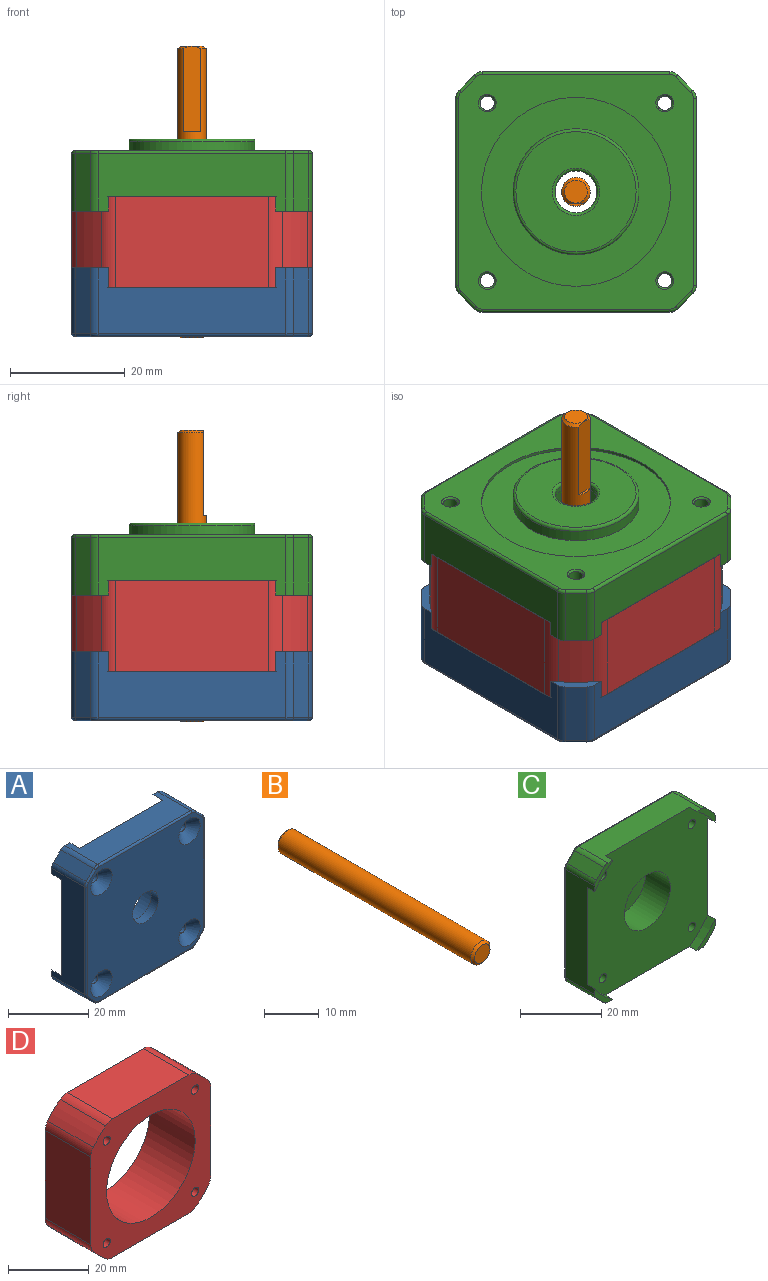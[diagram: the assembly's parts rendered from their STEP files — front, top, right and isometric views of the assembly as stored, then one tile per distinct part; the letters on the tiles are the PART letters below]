
ASSEMBLY  parts=4 mates=2
PART A: 53 faces, bbox 42.3x12x42.3 mm
  f0: cylinder r=4.5mm len=9mm, axis (0,-1,0), area 70.7mm2, adj f10,f28
  f1: plane 32.74x11.5mm, normal (0,0,1), area 274.1mm2, adj f9,f11,f13,f14,f16,f30,f31,f50
  f2: plane 32.74x11.5mm, normal (1,0,0), area 274.1mm2, adj f9,f11,f13,f20,f22,f29,f36,f42
  f3: plane 32.74x11.5mm, normal (0,0,-1), area 274.1mm2, adj f9,f17,f19,f20,f22,f34,f35,f39
  f4: plane 32.74x11.5mm, normal (-1,0,0), area 274.1mm2, adj f9,f14,f16,f17,f19,f32,f33,f47
  f5: cylinder r=1.25mm len=6mm, axis (0,-1,0), area 47.1mm2, adj f9,f26
  f6: cylinder r=1.25mm len=6mm, axis (0,-1,0), area 47.1mm2, adj f9,f25
  f7: cylinder r=1.25mm len=6mm, axis (0,-1,0), area 47.1mm2, adj f9,f24
  f8: cylinder r=1.25mm len=6mm, axis (0,-1,0), area 47.1mm2, adj f9,f23
  f9: plane 42x42mm, normal (0,1,0), area 1472mm2, adj f1,f2,f3,f4,f5,f6,f7,f8
  f10: plane 41x41mm, normal (0,-1,0), area 1415.7mm2, adj f0,f23,f24,f25,f26,f37,f38,f39
  f11: cylinder r=25.6mm len=6.36mm, axis (0,-1,0), area 31.6mm2, adj f1,f2,f9,f13
  f12: plane 11.5x2.63mm, normal (0.71,0,0.71), area 42.7mm2, adj f13,f29,f30,f46
  f13: plane 6.36x6.36mm, normal (0,1,0), area 10.4mm2, adj f1,f2,f11,f12,f29,f30
  f14: cylinder r=25.6mm len=6.36mm, axis (0,-1,0), area 31.6mm2, adj f1,f4,f9,f16
  f15: plane 11.5x2.63mm, normal (-0.71,0,0.71), area 42.7mm2, adj f16,f31,f32,f51
  f16: plane 6.36x6.36mm, normal (0,1,0), area 10.4mm2, adj f1,f4,f14,f15,f31,f32
  f17: cylinder r=25.6mm len=6.36mm, axis (0,-1,0), area 31.6mm2, adj f3,f4,f9,f19
  f18: plane 11.5x2.63mm, normal (-0.71,0,-0.71), area 42.7mm2, adj f19,f33,f34,f43
  f19: plane 6.36x6.36mm, normal (0,1,0), area 10.4mm2, adj f3,f4,f17,f18,f33,f34
  f20: cylinder r=25.6mm len=6.36mm, axis (0,-1,0), area 31.6mm2, adj f2,f3,f9,f22
  f21: plane 11.5x2.63mm, normal (0.71,0,-0.71), area 42.7mm2, adj f22,f35,f36,f38
  f22: plane 6.36x6.36mm, normal (0,1,0), area 10.4mm2, adj f2,f3,f20,f21,f35,f36
  f23: cone r=3.75mm half-angle=45deg, axis (0,-1,0), area 55.5mm2, adj f8,f10
  f24: cone r=3.75mm half-angle=45deg, axis (0,-1,0), area 55.5mm2, adj f7,f10
  f25: cone r=3.75mm half-angle=45deg, axis (0,-1,0), area 55.5mm2, adj f6,f10
  f26: cone r=3.75mm half-angle=45deg, axis (0,-1,0), area 55.5mm2, adj f5,f10
  f27: cylinder r=8mm len=16mm, axis (0,1,0), area 301.6mm2, adj f9,f28
  f28: plane 16x16mm, normal (0,1,0), area 137.4mm2, adj f0,f27
  f29: cylinder r=2mm len=11.5mm, axis (0,-1,0), area 18.1mm2, adj f2,f12,f13,f44
  f30: cylinder r=2mm len=11.5mm, axis (0,-1,0), area 18.1mm2, adj f1,f12,f13,f48
  f31: cylinder r=2mm len=11.5mm, axis (0,-1,0), area 18.1mm2, adj f1,f15,f16,f52
  f32: cylinder r=2mm len=11.5mm, axis (0,1,0), area 18.1mm2, adj f4,f15,f16,f49
  f33: cylinder r=2mm len=11.5mm, axis (0,-1,0), area 18.1mm2, adj f4,f18,f19,f45
  f34: cylinder r=2mm len=11.5mm, axis (0,-1,0), area 18.1mm2, adj f3,f18,f19,f41
  f35: cylinder r=2mm len=11.5mm, axis (0,-1,0), area 18.1mm2, adj f3,f21,f22,f37
  f36: cylinder r=2mm len=11.5mm, axis (0,1,0), area 18.1mm2, adj f2,f21,f22,f40
  f37: torus R=1.5mm, axis (0,1,0), area 1.1mm2, adj f10,f35,f38,f39
  f38: cylinder r=0.5mm len=2.98mm, axis (-0.71,0,-0.71), area 2.9mm2, adj f10,f21,f37,f40
  f39: cylinder r=0.5mm len=32.74mm, axis (-1,0,0), area 25.7mm2, adj f3,f10,f37,f41
  f40: torus R=1.5mm, axis (0,1,0), area 1.1mm2, adj f10,f36,f38,f42
  f41: torus R=1.5mm, axis (0,1,0), area 1.1mm2, adj f10,f34,f39,f43
  f42: cylinder r=0.5mm len=32.74mm, axis (0,0,-1), area 25.7mm2, adj f2,f10,f40,f44
  f43: cylinder r=0.5mm len=2.98mm, axis (-0.71,0,0.71), area 2.9mm2, adj f10,f18,f41,f45
  f44: torus R=1.5mm, axis (0,1,0), area 1.1mm2, adj f10,f29,f42,f46
  f45: torus R=1.5mm, axis (0,1,0), area 1.1mm2, adj f10,f33,f43,f47
  f46: cylinder r=0.5mm len=2.98mm, axis (0.71,0,-0.71), area 2.9mm2, adj f10,f12,f44,f48
  f47: cylinder r=0.5mm len=32.74mm, axis (0,0,1), area 25.7mm2, adj f4,f10,f45,f49
  f48: torus R=1.5mm, axis (0,1,0), area 1.1mm2, adj f10,f30,f46,f50
  f49: torus R=1.5mm, axis (0,1,0), area 1.1mm2, adj f10,f32,f47,f51
  f50: cylinder r=0.5mm len=32.74mm, axis (1,0,0), area 25.7mm2, adj f1,f10,f48,f52
  f51: cylinder r=0.5mm len=2.98mm, axis (0.71,0,0.71), area 2.9mm2, adj f10,f15,f49,f52
  f52: torus R=1.5mm, axis (0,1,0), area 1.1mm2, adj f10,f31,f50,f51
PART B: 7 faces, bbox 5x51x5 mm
  f0: cylinder r=2.5mm len=50mm, axis (0,-1,0), area 738.7mm2, adj f3,f4,f5,f6
  f1: plane 4x4mm, normal (0,1,0), area 12.6mm2, adj f6
  f2: plane 4x4mm, normal (0,-1,0), area 12.6mm2, adj f5
  f3: plane 15x3mm, normal (0,0,-1), area 44.5mm2, adj f0,f4,f6
  f4: plane 3x0.5mm, normal (0,1,0), area 1mm2, adj f0,f3
  f5: cone r=2.5mm half-angle=45deg, axis (0,1,0), area 10mm2, adj f0,f2
  f6: cone r=2mm half-angle=45deg, axis (0,-1,0), area 8.6mm2, adj f0,f1,f3
PART C: 59 faces, bbox 42.3x12.6x42.3 mm
  f0: cylinder r=3.65mm len=7.3mm, axis (0,-1,0), area 20.6mm2, adj f28,f53
  f1: plane 42x42mm, normal (0,-1,0), area 1472mm2, adj f2,f4,f6,f8,f9,f10,f11,f14
  f2: plane 32.74x10.1mm, normal (0,0,1), area 254.6mm2, adj f1,f19,f20,f21,f22,f30,f31,f51
  f3: plane 10.1x2.63mm, normal (0.71,0,0.71), area 37.5mm2, adj f22,f29,f30,f47
  f4: plane 32.74x10.1mm, normal (1,0,0), area 254.6mm2, adj f1,f21,f22,f25,f26,f29,f36,f43
  f5: plane 10.1x2.63mm, normal (0.71,0,-0.71), area 37.5mm2, adj f26,f35,f36,f39
  f6: plane 32.74x10.1mm, normal (0,0,-1), area 254.6mm2, adj f1,f23,f24,f25,f26,f34,f35,f38
  f7: plane 10.1x2.63mm, normal (-0.71,0,-0.71), area 37.5mm2, adj f24,f33,f34,f42
  f8: plane 32.74x10.1mm, normal (-1,0,0), area 254.6mm2, adj f1,f19,f20,f23,f24,f32,f33,f46
  f9: cylinder r=1.25mm len=7.7mm, axis (0,-1,0), area 60.5mm2, adj f1,f58
  f10: cylinder r=1.25mm len=7.7mm, axis (0,-1,0), area 60.5mm2, adj f1,f57
  f11: cylinder r=1.25mm len=7.7mm, axis (0,-1,0), area 60.5mm2, adj f1,f56
  f12: plane 10.1x2.63mm, normal (-0.71,0,0.71), area 37.5mm2, adj f20,f31,f32,f50
  f13: cylinder r=16.5mm len=33mm, axis (0,-1,0), area 51.8mm2, adj f15,f16
  f14: cylinder r=1.25mm len=7.7mm, axis (0,-1,0), area 60.5mm2, adj f1,f55
  f15: plane 41x41mm, normal (0,1,0), area 770.5mm2, adj f13,f37,f38,f39,f40,f41,f42,f43
  f16: plane 33x33mm, normal (0,1,0), area 475.2mm2, adj f13,f17
  f17: cylinder r=11mm len=22mm, axis (0,-1,0), area 138.2mm2, adj f16,f54
  f18: plane 21x21mm, normal (0,1,0), area 292.3mm2, adj f53,f54
  f19: cylinder r=25.6mm len=6.36mm, axis (0,1,0), area 23.5mm2, adj f1,f2,f8,f20
  f20: plane 6.36x6.36mm, normal (0,-1,0), area 10.4mm2, adj f2,f8,f12,f19,f31,f32
  f21: cylinder r=25.6mm len=6.36mm, axis (0,1,0), area 23.5mm2, adj f1,f2,f4,f22
  f22: plane 6.36x6.36mm, normal (0,-1,0), area 10.4mm2, adj f2,f3,f4,f21,f29,f30
  f23: cylinder r=25.6mm len=6.36mm, axis (0,1,0), area 23.5mm2, adj f1,f6,f8,f24
  f24: plane 6.36x6.36mm, normal (0,-1,0), area 10.4mm2, adj f6,f7,f8,f23,f33,f34
  f25: cylinder r=25.6mm len=6.36mm, axis (0,1,0), area 23.5mm2, adj f1,f4,f6,f26
  f26: plane 6.36x6.36mm, normal (0,-1,0), area 10.4mm2, adj f4,f5,f6,f25,f35,f36
  f27: cylinder r=8mm len=16mm, axis (0,-1,0), area 432.3mm2, adj f1,f28
  f28: plane 16x16mm, normal (0,-1,0), area 159.2mm2, adj f0,f27
  f29: cylinder r=2mm len=10.1mm, axis (0,-1,0), area 15.9mm2, adj f3,f4,f22,f45
  f30: cylinder r=2mm len=10.1mm, axis (0,-1,0), area 15.9mm2, adj f2,f3,f22,f49
  f31: cylinder r=2mm len=10.1mm, axis (0,-1,0), area 15.9mm2, adj f2,f12,f20,f52
  f32: cylinder r=2mm len=10.1mm, axis (0,1,0), area 15.9mm2, adj f8,f12,f20,f48
  f33: cylinder r=2mm len=10.1mm, axis (0,-1,0), area 15.9mm2, adj f7,f8,f24,f44
  f34: cylinder r=2mm len=10.1mm, axis (0,-1,0), area 15.9mm2, adj f6,f7,f24,f40
  f35: cylinder r=2mm len=10.1mm, axis (0,-1,0), area 15.9mm2, adj f5,f6,f26,f37
  f36: cylinder r=2mm len=10.1mm, axis (0,1,0), area 15.9mm2, adj f4,f5,f26,f41
  f37: torus R=1.5mm, axis (0,1,0), area 1.1mm2, adj f15,f35,f38,f39
  f38: cylinder r=0.5mm len=32.74mm, axis (1,0,0), area 25.7mm2, adj f6,f15,f37,f40
  f39: cylinder r=0.5mm len=2.98mm, axis (0.71,0,0.71), area 2.9mm2, adj f5,f15,f37,f41
  f40: torus R=1.5mm, axis (0,1,0), area 1.1mm2, adj f15,f34,f38,f42
  f41: torus R=1.5mm, axis (0,1,0), area 1.1mm2, adj f15,f36,f39,f43
  f42: cylinder r=0.5mm len=2.98mm, axis (0.71,0,-0.71), area 2.9mm2, adj f7,f15,f40,f44
  f43: cylinder r=0.5mm len=32.74mm, axis (0,0,1), area 25.7mm2, adj f4,f15,f41,f45
  f44: torus R=1.5mm, axis (0,1,0), area 1.1mm2, adj f15,f33,f42,f46
  f45: torus R=1.5mm, axis (0,1,0), area 1.1mm2, adj f15,f29,f43,f47
  f46: cylinder r=0.5mm len=32.74mm, axis (0,0,-1), area 25.7mm2, adj f8,f15,f44,f48
  f47: cylinder r=0.5mm len=2.98mm, axis (-0.71,0,0.71), area 2.9mm2, adj f3,f15,f45,f49
  f48: torus R=1.5mm, axis (0,1,0), area 1.1mm2, adj f15,f32,f46,f50
  f49: torus R=1.5mm, axis (0,1,0), area 1.1mm2, adj f15,f30,f47,f51
  f50: cylinder r=0.5mm len=2.98mm, axis (-0.71,0,-0.71), area 2.9mm2, adj f12,f15,f48,f52
  f51: cylinder r=0.5mm len=32.74mm, axis (-1,0,0), area 25.7mm2, adj f2,f15,f49,f52
  f52: torus R=1.5mm, axis (0,1,0), area 1.1mm2, adj f15,f31,f50,f51
  f53: torus R=4.15mm, axis (0,1,0), area 18.9mm2, adj f0,f18
  f54: torus R=10.5mm, axis (0,1,0), area 53.4mm2, adj f17,f18
  f55: cone r=1.25mm half-angle=45deg, axis (0,1,0), area 3.7mm2, adj f14,f15
  f56: cone r=1.25mm half-angle=45deg, axis (0,1,0), area 3.7mm2, adj f11,f15
  f57: cone r=1.25mm half-angle=45deg, axis (0,1,0), area 3.7mm2, adj f10,f15
  f58: cone r=1.25mm half-angle=45deg, axis (0,1,0), area 3.7mm2, adj f9,f15
PART D: 23 faces, bbox 42x16x42 mm
  f0: plane 42x42mm, normal (0,1,0), area 916.8mm2, adj f2,f3,f4,f5,f6,f7,f8,f9
  f1: plane 42x42mm, normal (0,-1,0), area 916.8mm2, adj f2,f3,f4,f5,f6,f7,f8,f9
  f2: cylinder r=25.6mm len=16mm, axis (0,-1,0), area 98.8mm2, adj f0,f1,f17,f18
  f3: plane 26.65x16mm, normal (0,0,-1), area 426.4mm2, adj f0,f1,f16,f17
  f4: cylinder r=25.6mm len=16mm, axis (0,-1,0), area 98.8mm2, adj f0,f1,f15,f16
  f5: plane 26.65x16mm, normal (-1,0,0), area 426.4mm2, adj f0,f1,f15,f22
  f6: cylinder r=25.6mm len=16mm, axis (0,-1,0), area 98.8mm2, adj f0,f1,f21,f22
  f7: plane 26.65x16mm, normal (0,0,1), area 426.4mm2, adj f0,f1,f20,f21
  f8: cylinder r=25.6mm len=16mm, axis (0,-1,0), area 98.8mm2, adj f0,f1,f19,f20
  f9: plane 26.65x16mm, normal (1,0,0), area 426.4mm2, adj f0,f1,f18,f19
  f10: cylinder r=15.5mm len=31mm, axis (0,-1,0), area 1558.2mm2, adj f0,f1
  f11: cylinder r=1.25mm len=16mm, axis (0,-1,0), area 125.7mm2, adj f0,f1
  f12: cylinder r=1.25mm len=16mm, axis (0,-1,0), area 125.7mm2, adj f0,f1
  f13: cylinder r=1.25mm len=16mm, axis (0,-1,0), area 125.7mm2, adj f0,f1
  f14: cylinder r=1.25mm len=16mm, axis (0,-1,0), area 125.7mm2, adj f0,f1
  f15: cylinder r=4mm len=16mm, axis (0,-1,0), area 42.5mm2, adj f0,f1,f4,f5
  f16: cylinder r=4mm len=16mm, axis (0,-1,0), area 42.5mm2, adj f0,f1,f3,f4
  f17: cylinder r=4mm len=16mm, axis (0,-1,0), area 42.5mm2, adj f0,f1,f2,f3
  f18: cylinder r=4mm len=16mm, axis (0,-1,0), area 42.5mm2, adj f0,f1,f2,f9
  f19: cylinder r=4mm len=16mm, axis (0,-1,0), area 42.5mm2, adj f0,f1,f8,f9
  f20: cylinder r=4mm len=16mm, axis (0,-1,0), area 42.5mm2, adj f0,f1,f7,f8
  f21: cylinder r=4mm len=16mm, axis (0,-1,0), area 42.5mm2, adj f0,f1,f6,f7
  f22: cylinder r=4mm len=16mm, axis (0,-1,0), area 42.5mm2, adj f0,f1,f5,f6
PLACE A rot(axis=(0.58,0.58,0.58),120deg) t=(28.2,89.33,-92.42)mm
PLACE B rot(axis=(0.01,-0.71,-0.71),179.4deg) t=(28.2,89.33,-92.67)mm
PLACE C rot(axis=(1,0,0),90deg) t=(28.2,89.33,-67.92)mm
PLACE D rot(axis=(0,-0.71,0.71),180deg) t=(28.2,89.33,-67.92)mm
MATE revolute A.f0 <-> B.f0  axis (0,0,-1) through (28.2,89.33,-92.42)mm
MATE fastened D.f2 <-> C.f0  axis (0,0,1) through (28.2,89.33,-67.92)mm
